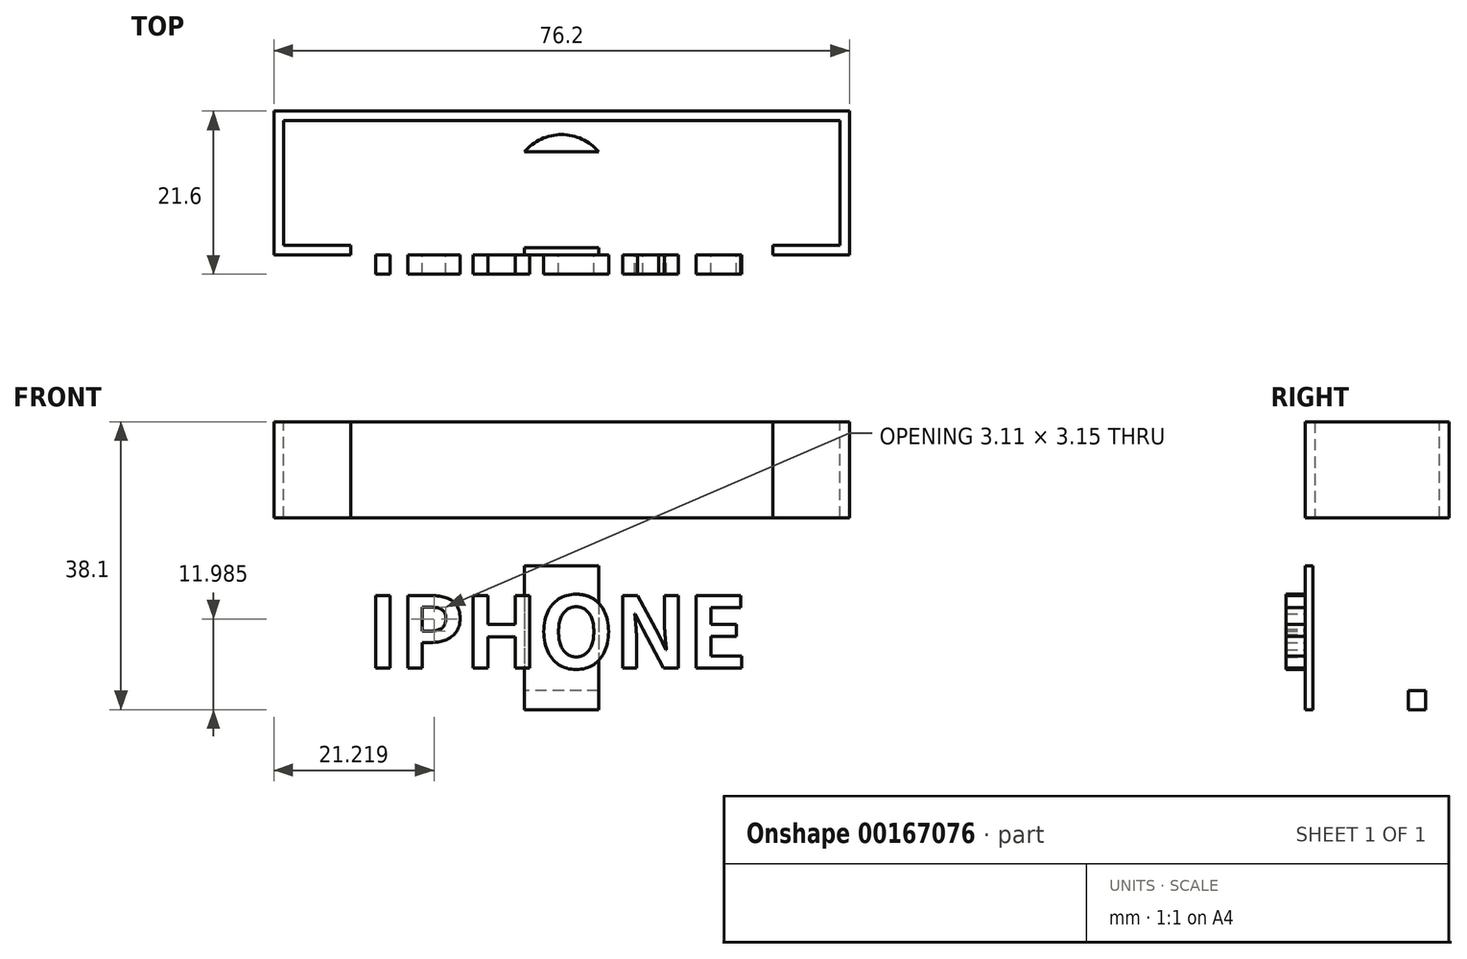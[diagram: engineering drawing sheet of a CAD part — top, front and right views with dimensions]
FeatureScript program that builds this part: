
annotation { "Feature Type Name" : "Feature", "Feature Type Description" : "" }
export const myFeature = defineFeature(function(context is Context, id is Id, definition is map)
    precondition{}
    {
        {
            var Q0;
            Q0=qCreatedBy(makeId("Top.planeOp"),FACE);
            var sketch = newSketch(context, id + "F0", { "sketchPlane" : qUnion([Q0])});
            skLineSegment(sketch, "E0.bottom", {"start": v(-38.1, 9.52) * mm, "end": v(38.1, 9.52) * mm});
            skLineSegment(sketch, "E0.top", {"start": v(-38.1, -9.52) * mm, "end": v(38.1, -9.52) * mm});
            skLineSegment(sketch, "E0.left", {"start": v(-38.1, 9.52) * mm, "end": v(-38.1, -9.52) * mm});
            skLineSegment(sketch, "E0.right", {"start": v(38.1, 9.52) * mm, "end": v(38.1, -9.52) * mm});
            skPoint(sketch, "E0.middle", {"position": v(0, 0) * mm});
            skSolve(sketch);
        }
        {
            var Q0;
            Q0=makeQuery(id+"F0.imprint","IMPRINT",FACE,{"disambiguationData":[TD([[makeQuery(id+"F0.imprint","IMPRINT",EDGE,{"derivedFrom":sQuery(id+"F0.wireOp",EDGE,"E0.bottom")}),-1.0]])]});
            extrude(context, id + "F1", {"entities" : qUnion([Q0]), "depth" : 38.1 * mm});
        }
        {
            var Q0;
            Q0=makeQuery(id+"F1.opExtrude","CAP_FACE",FACE,{"disambiguationData":[OSD([sQuery(id+"F0.wireOp",EDGE,"E0.bottom"),sQuery(id+"F0.wireOp",EDGE,"E0.top"),sQuery(id+"F0.wireOp",EDGE,"E0.left"),sQuery(id+"F0.wireOp",EDGE,"E0.right")])],"isStart":false});
            var sketch = newSketch(context, id + "F2", { "sketchPlane" : qUnion([Q0])});
            skLineSegment(sketch, "E1", {"start": v(-36.83, -8.25) * mm, "end": v(36.83, -8.25) * mm});
            skLineSegment(sketch, "E2", {"start": v(36.83, -8.25) * mm, "end": v(36.83, 8.26) * mm});
            skLineSegment(sketch, "E3", {"start": v(36.83, 8.26) * mm, "end": v(-36.83, 8.26) * mm});
            skLineSegment(sketch, "E4", {"start": v(-36.83, 8.26) * mm, "end": v(-36.83, -8.25) * mm});
            skSolve(sketch);
        }
        {
            var Q0;
            Q0=makeQuery(id+"F2.imprint","IMPRINT",FACE,{"disambiguationData":[TD([[makeQuery(id+"F2.imprint","IMPRINT",EDGE,{"derivedFrom":sQuery(id+"F2.wireOp",EDGE,"E1")}),1.0]])]});
            extrude(context, id + "F3", {"entities" : qUnion([Q0]), "operationType" : NewBodyOperationType.REMOVE, "oppositeDirection" : true, "depth" : 35.56 * mm});
        }
        {
            var Q0;
            Q0=makeQuery(id+"F1.opExtrude","SWEPT_FACE",FACE,{"disambiguationData":[OSD([sQuery(id+"F0.wireOp",EDGE,"E0.top")])]});
            var sketch = newSketch(context, id + "F4", { "sketchPlane" : qUnion([Q0])});
            skLineSegment(sketch, "E5", {"start": v(-27.94, 38.1) * mm, "end": v(-27.94, 19.05) * mm});
            skLineSegment(sketch, "E6", {"start": v(-27.94, 19.05) * mm, "end": v(27.94, 19.05) * mm});
            skLineSegment(sketch, "E7", {"start": v(27.94, 19.05) * mm, "end": v(27.94, 38.1) * mm});
            skLineSegment(sketch, "E8", {"start": v(27.94, 38.1) * mm, "end": v(-27.94, 38.1) * mm});
            skLineSegment(sketch, "E9", {"start": v(27.94, 38.1) * mm, "end": v(38.1, 38.1) * mm});
            skLineSegment(sketch, "E10", {"start": v(-38.1, 38.1) * mm, "end": v(-27.94, 38.1) * mm});
            skSolve(sketch);
        }
        {
            var Q0;
            Q0=makeQuery(id+"F4.imprint","IMPRINT",FACE,{"disambiguationData":[TD([[makeQuery(id+"F4.imprint","IMPRINT",EDGE,{"derivedFrom":sQuery(id+"F4.wireOp",EDGE,"E5")}),1.0]])]});
            extrude(context, id + "F5", {"entities" : qUnion([Q0]), "operationType" : NewBodyOperationType.REMOVE, "oppositeDirection" : true, "depth" : 2.54 * mm});
        }
        {
            var Q0;
            Q0=makeQuery(id+"F1.opExtrude","SWEPT_FACE",FACE,{"disambiguationData":[OSD([sQuery(id+"F0.wireOp",EDGE,"E0.top")])]});
            var sketch = newSketch(context, id + "F6", { "sketchPlane" : qUnion([Q0])});
            skText(sketch, "E11", { "text": "IPHONE", "fontName": "NotoSansCJKjp-Bold.otf"});
            const initialGuessF6  = {"E11": [-0.02582, 0.00548, 1, 0, 0.00934]};
            skSetInitialGuess(sketch, initialGuessF6);
            skSolve(sketch);
        }
        {
            var Q0;
            Q0 = qSketchRegion(id + "F6", true);
            extrude(context, id + "F7", {"entities" : qUnion([Q0]), "operationType" : NewBodyOperationType.ADD, "depth" : 2.54 * mm});
        }
        {
            var Q0;
            Q0=makeQuery(id+"F1.opExtrude","CAP_FACE",FACE,{"disambiguationData":[OSD([sQuery(id+"F0.wireOp",EDGE,"E0.bottom"),sQuery(id+"F0.wireOp",EDGE,"E0.top"),sQuery(id+"F0.wireOp",EDGE,"E0.left"),sQuery(id+"F0.wireOp",EDGE,"E0.right")])],"isStart":true});
            var sketch = newSketch(context, id + "F8", { "sketchPlane" : qUnion([Q0])});
            skCircle(sketch, "E12", {"center": v(0, 0) * mm, "radius": 6.42 * mm});
            skLineSegment(sketch, "E13.bottom", {"start": v(-4.91, 4.14) * mm, "end": v(4.91, 4.14) * mm});
            skLineSegment(sketch, "E13.top", {"start": v(-4.91, -4.14) * mm, "end": v(4.91, -4.14) * mm});
            skLineSegment(sketch, "E13.left", {"start": v(-4.91, 4.14) * mm, "end": v(-4.91, -4.14) * mm});
            skLineSegment(sketch, "E13.right", {"start": v(4.91, 4.14) * mm, "end": v(4.91, -4.14) * mm});
            skLineSegment(sketch, "E14", {"start": v(4.91, 4.14) * mm, "end": v(4.91, 9.52) * mm});
            skLineSegment(sketch, "E15", {"start": v(-4.91, 4.14) * mm, "end": v(-4.91, 9.52) * mm});
            skLineSegment(sketch, "E16", {"start": v(-4.91, 8.53) * mm, "end": v(4.91, 8.53) * mm});
            skSolve(sketch);
        }
        {
            var Q0;
            Q0=makeQuery(id+"F8.imprint","IMPRINT",FACE,{"disambiguationData":[TD([[makeQuery(id+"F8.imprint","IMPRINT",EDGE,{"derivedFrom":sQuery(id+"F8.wireOp",EDGE,"E13.bottom")}),-1.0]])]});
            var Q1;
            {var subQ0=sQuery(id+"F8.wireOp",EDGE,"E14");Q1=makeQuery(id+"F8.imprint","IMPRINT",FACE,{"disambiguationData":[TD([[makeQuery(id+"F8.imprint","IMPRINT",EDGE,{"derivedFrom":subQ0}),-1.0]])]});}
            var Q2;
            {var subQ0=sQuery(id+"F8.wireOp",EDGE,"E15");Q2=makeQuery(id+"F8.imprint","IMPRINT",FACE,{"disambiguationData":[TD([[makeQuery(id+"F8.imprint","IMPRINT",EDGE,{"derivedFrom":subQ0}),1.0]])]});}
            var Q3;
            {var subQ0=sQuery(id+"F8.wireOp",EDGE,"E13.left");Q3=makeQuery(id+"F8.imprint","IMPRINT",FACE,{"disambiguationData":[TD([[makeQuery(id+"F8.imprint","IMPRINT",EDGE,{"derivedFrom":subQ0}),-1.0]])]});}
            var Q4;
            {var subQ0=sQuery(id+"F8.wireOp",EDGE,"E13.right");Q4=makeQuery(id+"F8.imprint","IMPRINT",FACE,{"disambiguationData":[TD([[makeQuery(id+"F8.imprint","IMPRINT",EDGE,{"derivedFrom":subQ0}),1.0]])]});}
            var Q5;
            {var subQ0=sQuery(id+"F8.wireOp",EDGE,"E13.bottom");Q5=makeQuery(id+"F8.imprint","IMPRINT",FACE,{"disambiguationData":[TD([[makeQuery(id+"F8.imprint","IMPRINT",EDGE,{"derivedFrom":subQ0}),1.0]])]});}
            var Q6;
            {var subQ6=sQuery(id+"F8.wireOp",EDGE,"E16");Q6=makeQuery(id+"F8.imprint","IMPRINT",FACE,{"disambiguationData":[TD([[makeQuery(id+"F8.imprint","IMPRINT",EDGE,{"derivedFrom":subQ6}),-1.0]])]});}
            extrude(context, id + "F9", {"entities" : qUnion([Q0, Q1, Q2, Q3, Q4, Q5, Q6]), "operationType" : NewBodyOperationType.REMOVE, "oppositeDirection" : true, "depth" : 25.4 * mm});
        }
    });
